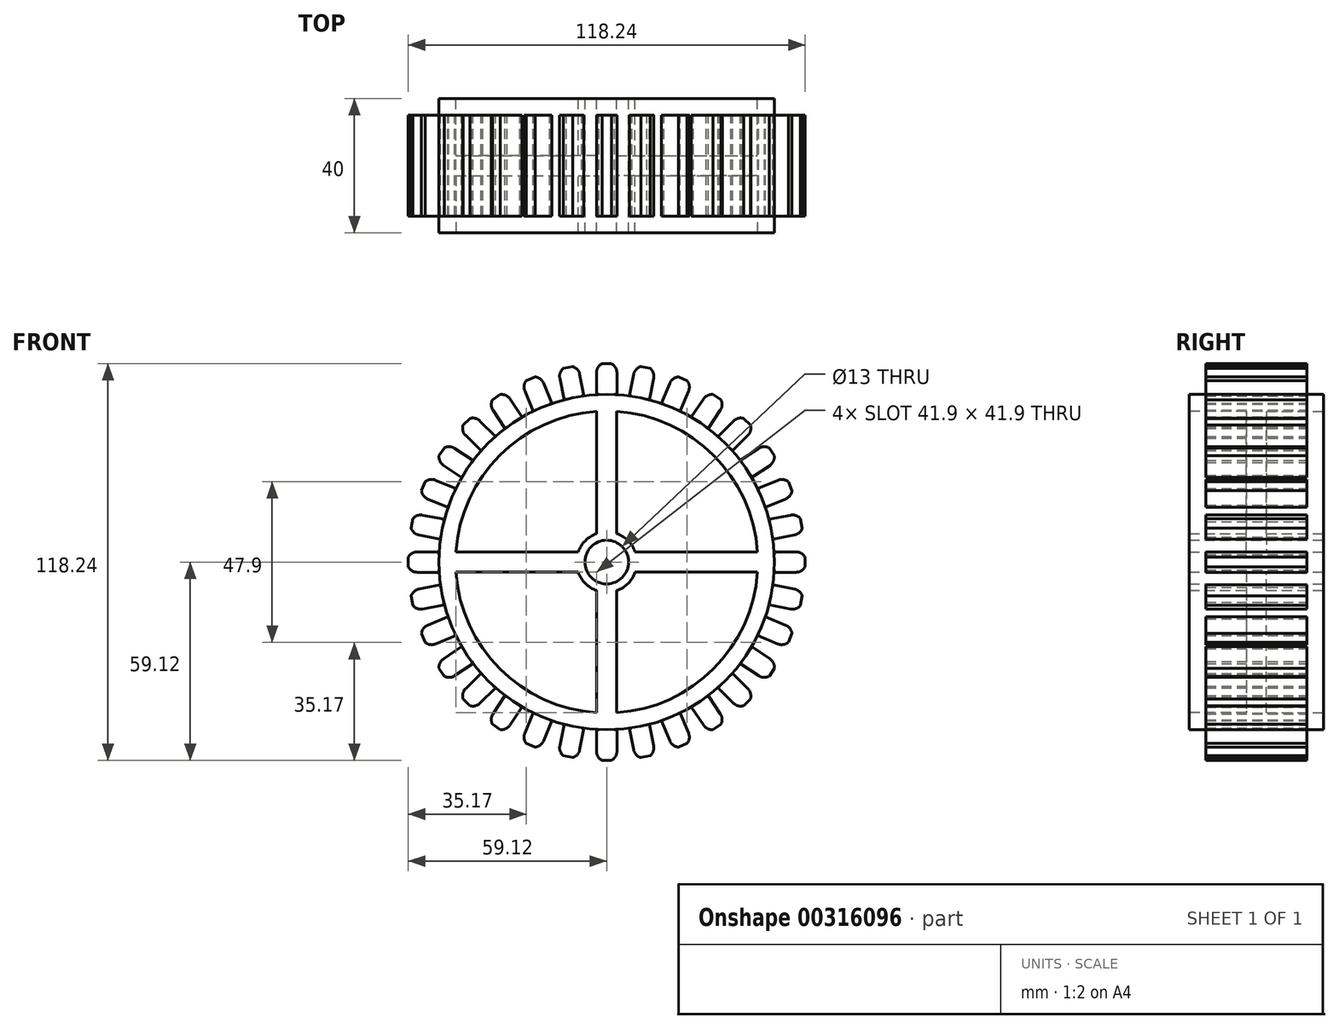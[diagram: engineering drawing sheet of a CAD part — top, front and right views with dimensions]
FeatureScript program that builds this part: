
annotation { "Feature Type Name" : "Feature", "Feature Type Description" : "" }
export const myFeature = defineFeature(function(context is Context, id is Id, definition is map)
    precondition{}
    {
        {
            var Q0;
            Q0=qCreatedBy(makeId("Front.planeOp"),FACE);
            var sketch = newSketch(context, id + "F0", { "sketchPlane" : qUnion([Q0])});
            skCircle(sketch, "E0", {"center": v(0, 0) * mm, "radius": 50 * mm});
            skSolve(sketch);
        }
        {
            var Q0;
            Q0 = qSketchRegion(id + "F0", true);
            extrude(context, id + "F1", {"entities" : qUnion([Q0]), "endBound" : BoundingType.SYMMETRIC, "depth" : 40 * mm});
        }
        {
            var Q0;
            Q0=makeQuery(id+"F1.opExtrude","CAP_FACE",FACE,{"disambiguationData":[OSD([sQuery(id+"F0.wireOp",EDGE,"E0")])],"isStart":false});
            var sketch = newSketch(context, id + "F2", { "sketchPlane" : qUnion([Q0])});
            skArc(sketch, "E1", {"start": v(-44.9, -3) * mm, "mid": v(-31.82, -31.82) * mm, "end": v(-3, -44.9) * mm});
            skLineSegment(sketch, "E2", {"start": v(-44.9, 3) * mm, "end": v(-3, 3) * mm});
            skLineSegment(sketch, "E3", {"start": v(-44.9, -3) * mm, "end": v(-3, -3) * mm});
            skLineSegment(sketch, "E4", {"start": v(-3, 44.9) * mm, "end": v(-3, 3) * mm});
            skLineSegment(sketch, "E5", {"start": v(3, 44.9) * mm, "end": v(3, 3) * mm});
            skArc(sketch, "E6.trimOffspring", {"start": v(-3, 44.9) * mm, "mid": v(-31.82, 31.82) * mm, "end": v(-44.9, 3) * mm});
            skArc(sketch, "E7.trimOffspring", {"start": v(44.9, 3) * mm, "mid": v(31.82, 31.82) * mm, "end": v(3, 44.9) * mm});
            skLineSegment(sketch, "E8.trimOffspring", {"start": v(3, -3) * mm, "end": v(3, -44.9) * mm});
            skLineSegment(sketch, "E9.trimOffspring", {"start": v(3, 3) * mm, "end": v(44.9, 3) * mm});
            skLineSegment(sketch, "E10.trimOffspring", {"start": v(-3, -3) * mm, "end": v(-3, -44.9) * mm});
            skLineSegment(sketch, "E11.trimOffspring", {"start": v(3, -3) * mm, "end": v(44.9, -3) * mm});
            skArc(sketch, "E12.trimOffspring", {"start": v(3, -44.9) * mm, "mid": v(31.82, -31.82) * mm, "end": v(44.9, -3) * mm});
            skLineSegment(sketch, "E13", {"start": v(-3.24, 3) * mm, "end": v(-3, 3.24) * mm});
            skPoint(sketch, "E14.orphan", {"position": v(31.82, 31.82) * mm});
            skPoint(sketch, "E15.orphan", {"position": v(-31.82, -31.82) * mm});
            skSolve(sketch);
        }
        {
            var Q0;
            Q0 = qSketchRegion(id + "F2", true);
            extrude(context, id + "F3", {"entities" : qUnion([Q0]), "operationType" : NewBodyOperationType.REMOVE, "oppositeDirection" : true, "depth" : 17 * mm});
        }
        {
            var Q0;
            Q0=makeQuery(id+"F1.opExtrude","CAP_FACE",FACE,{"disambiguationData":[OSD([sQuery(id+"F0.wireOp",EDGE,"E0")])],"isStart":true});
            var sketch = newSketch(context, id + "F4", { "sketchPlane" : qUnion([Q0])});
            skArc(sketch, "E16", {"start": v(3, -44.9) * mm, "mid": v(31.82, -31.82) * mm, "end": v(44.9, -3) * mm});
            skLineSegment(sketch, "E17", {"start": v(44.9, -3) * mm, "end": v(3, -3) * mm});
            skLineSegment(sketch, "E18", {"start": v(44.9, 3) * mm, "end": v(3, 3) * mm});
            skLineSegment(sketch, "E19", {"start": v(3, -44.9) * mm, "end": v(3, -3) * mm});
            skLineSegment(sketch, "E20", {"start": v(-3, -44.9) * mm, "end": v(-3, -3) * mm});
            skArc(sketch, "E21.trimOffspring", {"start": v(-44.9, -3) * mm, "mid": v(-31.82, -31.82) * mm, "end": v(-3, -44.9) * mm});
            skLineSegment(sketch, "E22.trimOffspring", {"start": v(-3, 3) * mm, "end": v(-3, 44.9) * mm});
            skLineSegment(sketch, "E23.trimOffspring", {"start": v(-3, -3) * mm, "end": v(-44.9, -3) * mm});
            skLineSegment(sketch, "E24.trimOffspring", {"start": v(3, 3) * mm, "end": v(3, 44.9) * mm});
            skLineSegment(sketch, "E25.trimOffspring", {"start": v(-3, 3) * mm, "end": v(-44.9, 3) * mm});
            skArc(sketch, "E26.trimOffspring", {"start": v(44.9, 3) * mm, "mid": v(31.82, 31.82) * mm, "end": v(3, 44.9) * mm});
            skArc(sketch, "E27.trimOffspring", {"start": v(-3, 44.9) * mm, "mid": v(-31.82, 31.82) * mm, "end": v(-44.9, 3) * mm});
            skSolve(sketch);
        }
        {
            var Q0;
            Q0 = qSketchRegion(id + "F4", true);
            var Q1;
            Q1 = qSketchRegion(id + "F6", true);
            extrude(context, id + "F5", {"entities" : qUnion([Q0, Q1]), "operationType" : NewBodyOperationType.REMOVE, "oppositeDirection" : true, "depth" : 17 * mm});
        }
        {
            var Q0;
            Q0=qCreatedBy(makeId("Front.planeOp"),FACE);
            var sketch = newSketch(context, id + "F6", { "sketchPlane" : qUnion([Q0])});
            skLineSegment(sketch, "E28.bottom", {"start": v(-3.03, 49.95) * mm, "end": v(0, 49.95) * mm});
            skLineSegment(sketch, "E28.left", {"start": v(-3.03, 49.95) * mm, "end": v(-3.03, 56.44) * mm});
            skArc(sketch, "E29", {"start": v(-3.03, 56.44) * mm, "mid": v(-2.6, 58) * mm, "end": v(-1.42, 59.12) * mm});
            skLineSegment(sketch, "E30", {"start": v(-1.42, 59.12) * mm, "end": v(0, 59.12) * mm});
            skPoint(sketch, "E31.orphan", {"position": v(0, 59.47) * mm});
            skArc(sketch, "E32.MirrorCS", {"start": v(3.03, 56.44) * mm, "mid": v(2.6, 58) * mm, "end": v(1.42, 59.12) * mm});
            skLineSegment(sketch, "E33.MirrorCS", {"start": v(1.42, 59.12) * mm, "end": v(0, 59.12) * mm});
            skLineSegment(sketch, "E34.MirrorCS", {"start": v(3.03, 49.95) * mm, "end": v(0, 49.95) * mm});
            skLineSegment(sketch, "E35.MirrorCS", {"start": v(3.03, 49.95) * mm, "end": v(3.03, 56.44) * mm});
            skLineSegment(sketch, "E36.1.0", {"start": v(-12.72, 48.4) * mm, "end": v(-13.99, 54.77) * mm});
            skLineSegment(sketch, "E36.1.1", {"start": v(-12.93, 57.7) * mm, "end": v(-11.53, 57.98) * mm});
            skLineSegment(sketch, "E36.1.2", {"start": v(-12.72, 48.4) * mm, "end": v(-9.74, 48.99) * mm});
            skArc(sketch, "E36.1.3", {"start": v(-13.99, 54.77) * mm, "mid": v(-13.87, 56.38) * mm, "end": v(-12.93, 57.7) * mm});
            skArc(sketch, "E36.1.4", {"start": v(-8.04, 55.95) * mm, "mid": v(-8.77, 57.4) * mm, "end": v(-10.14, 58.26) * mm});
            skPoint(sketch, "E36.1.5", {"position": v(-11.6, 58.33) * mm});
            skLineSegment(sketch, "E36.1.6", {"start": v(-6.77, 49.58) * mm, "end": v(-9.74, 48.99) * mm});
            skLineSegment(sketch, "E36.1.7", {"start": v(-6.77, 49.58) * mm, "end": v(-8.04, 55.95) * mm});
            skPoint(sketch, "E36.1.8", {"position": v(-11.6, 58.33) * mm});
            skLineSegment(sketch, "E36.1.9", {"start": v(-10.14, 58.26) * mm, "end": v(-11.53, 57.98) * mm});
            skLineSegment(sketch, "E36.2.0", {"start": v(-21.92, 44.98) * mm, "end": v(-24.4, 50.98) * mm});
            skLineSegment(sketch, "E36.2.1", {"start": v(-23.94, 54.07) * mm, "end": v(-22.62, 54.62) * mm});
            skLineSegment(sketch, "E36.2.2", {"start": v(-21.92, 44.98) * mm, "end": v(-19.11, 46.15) * mm});
            skArc(sketch, "E36.2.3", {"start": v(-24.4, 50.98) * mm, "mid": v(-24.6, 52.6) * mm, "end": v(-23.94, 54.07) * mm});
            skArc(sketch, "E36.2.4", {"start": v(-18.8, 53.3) * mm, "mid": v(-19.8, 54.58) * mm, "end": v(-21.3, 55.16) * mm});
            skPoint(sketch, "E36.2.5", {"position": v(-22.76, 54.95) * mm});
            skLineSegment(sketch, "E36.2.6", {"start": v(-16.31, 47.3) * mm, "end": v(-19.11, 46.15) * mm});
            skLineSegment(sketch, "E36.2.7", {"start": v(-16.31, 47.3) * mm, "end": v(-18.8, 53.3) * mm});
            skPoint(sketch, "E36.2.8", {"position": v(-22.76, 54.95) * mm});
            skLineSegment(sketch, "E36.2.9", {"start": v(-21.3, 55.16) * mm, "end": v(-22.62, 54.62) * mm});
            skLineSegment(sketch, "E36.3.0", {"start": v(-30.27, 39.85) * mm, "end": v(-33.88, 45.24) * mm});
            skLineSegment(sketch, "E36.3.1", {"start": v(-34.03, 48.36) * mm, "end": v(-32.84, 49.16) * mm});
            skLineSegment(sketch, "E36.3.2", {"start": v(-30.27, 39.85) * mm, "end": v(-27.75, 41.53) * mm});
            skArc(sketch, "E36.3.3", {"start": v(-33.88, 45.24) * mm, "mid": v(-34.39, 46.78) * mm, "end": v(-34.03, 48.36) * mm});
            skArc(sketch, "E36.3.4", {"start": v(-28.84, 48.61) * mm, "mid": v(-30.06, 49.67) * mm, "end": v(-31.66, 49.95) * mm});
            skPoint(sketch, "E36.3.5", {"position": v(-33.04, 49.45) * mm});
            skLineSegment(sketch, "E36.3.6", {"start": v(-25.23, 43.21) * mm, "end": v(-27.75, 41.53) * mm});
            skLineSegment(sketch, "E36.3.7", {"start": v(-25.23, 43.21) * mm, "end": v(-28.84, 48.61) * mm});
            skPoint(sketch, "E36.3.8", {"position": v(-33.04, 49.45) * mm});
            skLineSegment(sketch, "E36.3.9", {"start": v(-31.66, 49.95) * mm, "end": v(-32.84, 49.16) * mm});
            skLineSegment(sketch, "E36.4.0", {"start": v(-37.46, 33.17) * mm, "end": v(-42.05, 37.77) * mm});
            skLineSegment(sketch, "E36.4.1", {"start": v(-42.8, 40.8) * mm, "end": v(-41.8, 41.8) * mm});
            skLineSegment(sketch, "E36.4.2", {"start": v(-37.46, 33.17) * mm, "end": v(-35.32, 35.32) * mm});
            skArc(sketch, "E36.4.3", {"start": v(-42.05, 37.77) * mm, "mid": v(-42.85, 39.18) * mm, "end": v(-42.8, 40.8) * mm});
            skArc(sketch, "E36.4.4", {"start": v(-37.77, 42.05) * mm, "mid": v(-39.18, 42.85) * mm, "end": v(-40.8, 42.8) * mm});
            skPoint(sketch, "E36.4.5", {"position": v(-42.05, 42.05) * mm});
            skLineSegment(sketch, "E36.4.6", {"start": v(-33.17, 37.46) * mm, "end": v(-35.32, 35.32) * mm});
            skLineSegment(sketch, "E36.4.7", {"start": v(-33.17, 37.46) * mm, "end": v(-37.77, 42.05) * mm});
            skPoint(sketch, "E36.4.8", {"position": v(-42.05, 42.05) * mm});
            skLineSegment(sketch, "E36.4.9", {"start": v(-40.8, 42.8) * mm, "end": v(-41.8, 41.8) * mm});
            skLineSegment(sketch, "E36.5.0", {"start": v(-43.21, 25.23) * mm, "end": v(-48.61, 28.84) * mm});
            skLineSegment(sketch, "E36.5.1", {"start": v(-49.95, 31.66) * mm, "end": v(-49.16, 32.84) * mm});
            skLineSegment(sketch, "E36.5.2", {"start": v(-43.21, 25.23) * mm, "end": v(-41.53, 27.75) * mm});
            skArc(sketch, "E36.5.3", {"start": v(-48.61, 28.84) * mm, "mid": v(-49.67, 30.06) * mm, "end": v(-49.95, 31.66) * mm});
            skArc(sketch, "E36.5.4", {"start": v(-45.24, 33.88) * mm, "mid": v(-46.78, 34.39) * mm, "end": v(-48.36, 34.03) * mm});
            skPoint(sketch, "E36.5.5", {"position": v(-49.45, 33.04) * mm});
            skLineSegment(sketch, "E36.5.6", {"start": v(-39.85, 30.27) * mm, "end": v(-41.53, 27.75) * mm});
            skLineSegment(sketch, "E36.5.7", {"start": v(-39.85, 30.27) * mm, "end": v(-45.24, 33.88) * mm});
            skPoint(sketch, "E36.5.8", {"position": v(-49.45, 33.04) * mm});
            skLineSegment(sketch, "E36.5.9", {"start": v(-48.36, 34.03) * mm, "end": v(-49.16, 32.84) * mm});
            skLineSegment(sketch, "E36.6.0", {"start": v(-47.3, 16.31) * mm, "end": v(-53.3, 18.8) * mm});
            skLineSegment(sketch, "E36.6.1", {"start": v(-55.16, 21.3) * mm, "end": v(-54.62, 22.62) * mm});
            skLineSegment(sketch, "E36.6.2", {"start": v(-47.3, 16.31) * mm, "end": v(-46.15, 19.11) * mm});
            skArc(sketch, "E36.6.3", {"start": v(-53.3, 18.8) * mm, "mid": v(-54.58, 19.8) * mm, "end": v(-55.16, 21.3) * mm});
            skArc(sketch, "E36.6.4", {"start": v(-50.98, 24.4) * mm, "mid": v(-52.6, 24.6) * mm, "end": v(-54.07, 23.94) * mm});
            skPoint(sketch, "E36.6.5", {"position": v(-54.95, 22.76) * mm});
            skLineSegment(sketch, "E36.6.6", {"start": v(-44.98, 21.92) * mm, "end": v(-46.15, 19.11) * mm});
            skLineSegment(sketch, "E36.6.7", {"start": v(-44.98, 21.92) * mm, "end": v(-50.98, 24.4) * mm});
            skPoint(sketch, "E36.6.8", {"position": v(-54.95, 22.76) * mm});
            skLineSegment(sketch, "E36.6.9", {"start": v(-54.07, 23.94) * mm, "end": v(-54.62, 22.62) * mm});
            skLineSegment(sketch, "E36.7.0", {"start": v(-49.58, 6.77) * mm, "end": v(-55.95, 8.04) * mm});
            skLineSegment(sketch, "E36.7.1", {"start": v(-58.26, 10.14) * mm, "end": v(-57.98, 11.53) * mm});
            skLineSegment(sketch, "E36.7.2", {"start": v(-49.58, 6.77) * mm, "end": v(-48.99, 9.74) * mm});
            skArc(sketch, "E36.7.3", {"start": v(-55.95, 8.04) * mm, "mid": v(-57.4, 8.77) * mm, "end": v(-58.26, 10.14) * mm});
            skArc(sketch, "E36.7.4", {"start": v(-54.77, 13.99) * mm, "mid": v(-56.38, 13.87) * mm, "end": v(-57.7, 12.93) * mm});
            skPoint(sketch, "E36.7.5", {"position": v(-58.33, 11.6) * mm});
            skLineSegment(sketch, "E36.7.6", {"start": v(-48.4, 12.72) * mm, "end": v(-48.99, 9.74) * mm});
            skLineSegment(sketch, "E36.7.7", {"start": v(-48.4, 12.72) * mm, "end": v(-54.77, 13.99) * mm});
            skPoint(sketch, "E36.7.8", {"position": v(-58.33, 11.6) * mm});
            skLineSegment(sketch, "E36.7.9", {"start": v(-57.7, 12.93) * mm, "end": v(-57.98, 11.53) * mm});
            skLineSegment(sketch, "E36.8.0", {"start": v(-49.95, -3.03) * mm, "end": v(-56.44, -3.03) * mm});
            skLineSegment(sketch, "E36.8.1", {"start": v(-59.12, -1.42) * mm, "end": v(-59.12, 0) * mm});
            skLineSegment(sketch, "E36.8.2", {"start": v(-49.95, -3.03) * mm, "end": v(-49.95, 0) * mm});
            skArc(sketch, "E36.8.3", {"start": v(-56.44, -3.03) * mm, "mid": v(-58, -2.6) * mm, "end": v(-59.12, -1.42) * mm});
            skArc(sketch, "E36.8.4", {"start": v(-56.44, 3.03) * mm, "mid": v(-58, 2.6) * mm, "end": v(-59.12, 1.42) * mm});
            skPoint(sketch, "E36.8.5", {"position": v(-59.47, 0) * mm});
            skLineSegment(sketch, "E36.8.6", {"start": v(-49.95, 3.03) * mm, "end": v(-49.95, 0) * mm});
            skLineSegment(sketch, "E36.8.7", {"start": v(-49.95, 3.03) * mm, "end": v(-56.44, 3.03) * mm});
            skPoint(sketch, "E36.8.8", {"position": v(-59.47, 0) * mm});
            skLineSegment(sketch, "E36.8.9", {"start": v(-59.12, 1.42) * mm, "end": v(-59.12, 0) * mm});
            skLineSegment(sketch, "E36.9.0", {"start": v(-48.4, -12.72) * mm, "end": v(-54.77, -13.99) * mm});
            skLineSegment(sketch, "E36.9.1", {"start": v(-57.7, -12.93) * mm, "end": v(-57.98, -11.53) * mm});
            skLineSegment(sketch, "E36.9.2", {"start": v(-48.4, -12.72) * mm, "end": v(-48.99, -9.74) * mm});
            skArc(sketch, "E36.9.3", {"start": v(-54.77, -13.99) * mm, "mid": v(-56.38, -13.87) * mm, "end": v(-57.7, -12.93) * mm});
            skArc(sketch, "E36.9.4", {"start": v(-55.95, -8.04) * mm, "mid": v(-57.4, -8.77) * mm, "end": v(-58.26, -10.14) * mm});
            skPoint(sketch, "E36.9.5", {"position": v(-58.33, -11.6) * mm});
            skLineSegment(sketch, "E36.9.6", {"start": v(-49.58, -6.77) * mm, "end": v(-48.99, -9.74) * mm});
            skLineSegment(sketch, "E36.9.7", {"start": v(-49.58, -6.77) * mm, "end": v(-55.95, -8.04) * mm});
            skPoint(sketch, "E36.9.8", {"position": v(-58.33, -11.6) * mm});
            skLineSegment(sketch, "E36.9.9", {"start": v(-58.26, -10.14) * mm, "end": v(-57.98, -11.53) * mm});
            skLineSegment(sketch, "E36.10.0", {"start": v(-44.98, -21.92) * mm, "end": v(-50.98, -24.4) * mm});
            skLineSegment(sketch, "E36.10.1", {"start": v(-54.07, -23.94) * mm, "end": v(-54.62, -22.62) * mm});
            skLineSegment(sketch, "E36.10.2", {"start": v(-44.98, -21.92) * mm, "end": v(-46.15, -19.11) * mm});
            skArc(sketch, "E36.10.3", {"start": v(-50.98, -24.4) * mm, "mid": v(-52.6, -24.6) * mm, "end": v(-54.07, -23.94) * mm});
            skArc(sketch, "E36.10.4", {"start": v(-53.3, -18.8) * mm, "mid": v(-54.58, -19.8) * mm, "end": v(-55.16, -21.3) * mm});
            skPoint(sketch, "E36.10.5", {"position": v(-54.95, -22.76) * mm});
            skLineSegment(sketch, "E36.10.6", {"start": v(-47.3, -16.31) * mm, "end": v(-46.15, -19.11) * mm});
            skLineSegment(sketch, "E36.10.7", {"start": v(-47.3, -16.31) * mm, "end": v(-53.3, -18.8) * mm});
            skPoint(sketch, "E36.10.8", {"position": v(-54.95, -22.76) * mm});
            skLineSegment(sketch, "E36.10.9", {"start": v(-55.16, -21.3) * mm, "end": v(-54.62, -22.62) * mm});
            skLineSegment(sketch, "E36.11.0", {"start": v(-39.85, -30.27) * mm, "end": v(-45.24, -33.88) * mm});
            skLineSegment(sketch, "E36.11.1", {"start": v(-48.36, -34.03) * mm, "end": v(-49.16, -32.84) * mm});
            skLineSegment(sketch, "E36.11.2", {"start": v(-39.85, -30.27) * mm, "end": v(-41.53, -27.75) * mm});
            skArc(sketch, "E36.11.3", {"start": v(-45.24, -33.88) * mm, "mid": v(-46.78, -34.39) * mm, "end": v(-48.36, -34.03) * mm});
            skArc(sketch, "E36.11.4", {"start": v(-48.61, -28.84) * mm, "mid": v(-49.67, -30.06) * mm, "end": v(-49.95, -31.66) * mm});
            skPoint(sketch, "E36.11.5", {"position": v(-49.45, -33.04) * mm});
            skLineSegment(sketch, "E36.11.6", {"start": v(-43.21, -25.23) * mm, "end": v(-41.53, -27.75) * mm});
            skLineSegment(sketch, "E36.11.7", {"start": v(-43.21, -25.23) * mm, "end": v(-48.61, -28.84) * mm});
            skPoint(sketch, "E36.11.8", {"position": v(-49.45, -33.04) * mm});
            skLineSegment(sketch, "E36.11.9", {"start": v(-49.95, -31.66) * mm, "end": v(-49.16, -32.84) * mm});
            skLineSegment(sketch, "E36.12.0", {"start": v(-33.17, -37.46) * mm, "end": v(-37.77, -42.05) * mm});
            skLineSegment(sketch, "E36.12.1", {"start": v(-40.8, -42.8) * mm, "end": v(-41.8, -41.8) * mm});
            skLineSegment(sketch, "E36.12.2", {"start": v(-33.17, -37.46) * mm, "end": v(-35.32, -35.32) * mm});
            skArc(sketch, "E36.12.3", {"start": v(-37.77, -42.05) * mm, "mid": v(-39.18, -42.85) * mm, "end": v(-40.8, -42.8) * mm});
            skArc(sketch, "E36.12.4", {"start": v(-42.05, -37.77) * mm, "mid": v(-42.85, -39.18) * mm, "end": v(-42.8, -40.8) * mm});
            skPoint(sketch, "E36.12.5", {"position": v(-42.05, -42.05) * mm});
            skLineSegment(sketch, "E36.12.6", {"start": v(-37.46, -33.17) * mm, "end": v(-35.32, -35.32) * mm});
            skLineSegment(sketch, "E36.12.7", {"start": v(-37.46, -33.17) * mm, "end": v(-42.05, -37.77) * mm});
            skPoint(sketch, "E36.12.8", {"position": v(-42.05, -42.05) * mm});
            skLineSegment(sketch, "E36.12.9", {"start": v(-42.8, -40.8) * mm, "end": v(-41.8, -41.8) * mm});
            skLineSegment(sketch, "E36.13.0", {"start": v(-25.23, -43.21) * mm, "end": v(-28.84, -48.61) * mm});
            skLineSegment(sketch, "E36.13.1", {"start": v(-31.66, -49.95) * mm, "end": v(-32.84, -49.16) * mm});
            skLineSegment(sketch, "E36.13.2", {"start": v(-25.23, -43.21) * mm, "end": v(-27.75, -41.53) * mm});
            skArc(sketch, "E36.13.3", {"start": v(-28.84, -48.61) * mm, "mid": v(-30.06, -49.67) * mm, "end": v(-31.66, -49.95) * mm});
            skArc(sketch, "E36.13.4", {"start": v(-33.88, -45.24) * mm, "mid": v(-34.39, -46.78) * mm, "end": v(-34.03, -48.36) * mm});
            skPoint(sketch, "E36.13.5", {"position": v(-33.04, -49.45) * mm});
            skLineSegment(sketch, "E36.13.6", {"start": v(-30.27, -39.85) * mm, "end": v(-27.75, -41.53) * mm});
            skLineSegment(sketch, "E36.13.7", {"start": v(-30.27, -39.85) * mm, "end": v(-33.88, -45.24) * mm});
            skPoint(sketch, "E36.13.8", {"position": v(-33.04, -49.45) * mm});
            skLineSegment(sketch, "E36.13.9", {"start": v(-34.03, -48.36) * mm, "end": v(-32.84, -49.16) * mm});
            skLineSegment(sketch, "E36.14.0", {"start": v(-16.31, -47.3) * mm, "end": v(-18.8, -53.3) * mm});
            skLineSegment(sketch, "E36.14.1", {"start": v(-21.3, -55.16) * mm, "end": v(-22.62, -54.62) * mm});
            skLineSegment(sketch, "E36.14.2", {"start": v(-16.31, -47.3) * mm, "end": v(-19.11, -46.15) * mm});
            skArc(sketch, "E36.14.3", {"start": v(-18.8, -53.3) * mm, "mid": v(-19.8, -54.58) * mm, "end": v(-21.3, -55.16) * mm});
            skArc(sketch, "E36.14.4", {"start": v(-24.4, -50.98) * mm, "mid": v(-24.6, -52.6) * mm, "end": v(-23.94, -54.07) * mm});
            skPoint(sketch, "E36.14.5", {"position": v(-22.76, -54.95) * mm});
            skLineSegment(sketch, "E36.14.6", {"start": v(-21.92, -44.98) * mm, "end": v(-19.11, -46.15) * mm});
            skLineSegment(sketch, "E36.14.7", {"start": v(-21.92, -44.98) * mm, "end": v(-24.4, -50.98) * mm});
            skPoint(sketch, "E36.14.8", {"position": v(-22.76, -54.95) * mm});
            skLineSegment(sketch, "E36.14.9", {"start": v(-23.94, -54.07) * mm, "end": v(-22.62, -54.62) * mm});
            skLineSegment(sketch, "E36.15.0", {"start": v(-6.77, -49.58) * mm, "end": v(-8.04, -55.95) * mm});
            skLineSegment(sketch, "E36.15.1", {"start": v(-10.14, -58.26) * mm, "end": v(-11.53, -57.98) * mm});
            skLineSegment(sketch, "E36.15.2", {"start": v(-6.77, -49.58) * mm, "end": v(-9.74, -48.99) * mm});
            skArc(sketch, "E36.15.3", {"start": v(-8.04, -55.95) * mm, "mid": v(-8.77, -57.4) * mm, "end": v(-10.14, -58.26) * mm});
            skArc(sketch, "E36.15.4", {"start": v(-13.99, -54.77) * mm, "mid": v(-13.87, -56.38) * mm, "end": v(-12.93, -57.7) * mm});
            skPoint(sketch, "E36.15.5", {"position": v(-11.6, -58.33) * mm});
            skLineSegment(sketch, "E36.15.6", {"start": v(-12.72, -48.4) * mm, "end": v(-9.74, -48.99) * mm});
            skLineSegment(sketch, "E36.15.7", {"start": v(-12.72, -48.4) * mm, "end": v(-13.99, -54.77) * mm});
            skPoint(sketch, "E36.15.8", {"position": v(-11.6, -58.33) * mm});
            skLineSegment(sketch, "E36.15.9", {"start": v(-12.93, -57.7) * mm, "end": v(-11.53, -57.98) * mm});
            skLineSegment(sketch, "E36.16.0", {"start": v(3.03, -49.95) * mm, "end": v(3.03, -56.44) * mm});
            skLineSegment(sketch, "E36.16.1", {"start": v(1.42, -59.12) * mm, "end": v(0, -59.12) * mm});
            skLineSegment(sketch, "E36.16.2", {"start": v(3.03, -49.95) * mm, "end": v(0, -49.95) * mm});
            skArc(sketch, "E36.16.3", {"start": v(3.03, -56.44) * mm, "mid": v(2.6, -58) * mm, "end": v(1.42, -59.12) * mm});
            skArc(sketch, "E36.16.4", {"start": v(-3.03, -56.44) * mm, "mid": v(-2.6, -58) * mm, "end": v(-1.42, -59.12) * mm});
            skPoint(sketch, "E36.16.5", {"position": v(0, -59.47) * mm});
            skLineSegment(sketch, "E36.16.6", {"start": v(-3.03, -49.95) * mm, "end": v(0, -49.95) * mm});
            skLineSegment(sketch, "E36.16.7", {"start": v(-3.03, -49.95) * mm, "end": v(-3.03, -56.44) * mm});
            skPoint(sketch, "E36.16.8", {"position": v(0, -59.47) * mm});
            skLineSegment(sketch, "E36.16.9", {"start": v(-1.42, -59.12) * mm, "end": v(0, -59.12) * mm});
            skLineSegment(sketch, "E36.17.0", {"start": v(12.72, -48.4) * mm, "end": v(13.99, -54.77) * mm});
            skLineSegment(sketch, "E36.17.1", {"start": v(12.93, -57.7) * mm, "end": v(11.53, -57.98) * mm});
            skLineSegment(sketch, "E36.17.2", {"start": v(12.72, -48.4) * mm, "end": v(9.74, -48.99) * mm});
            skArc(sketch, "E36.17.3", {"start": v(13.99, -54.77) * mm, "mid": v(13.87, -56.38) * mm, "end": v(12.93, -57.7) * mm});
            skArc(sketch, "E36.17.4", {"start": v(8.04, -55.95) * mm, "mid": v(8.77, -57.4) * mm, "end": v(10.14, -58.26) * mm});
            skPoint(sketch, "E36.17.5", {"position": v(11.6, -58.33) * mm});
            skLineSegment(sketch, "E36.17.6", {"start": v(6.77, -49.58) * mm, "end": v(9.74, -48.99) * mm});
            skLineSegment(sketch, "E36.17.7", {"start": v(6.77, -49.58) * mm, "end": v(8.04, -55.95) * mm});
            skPoint(sketch, "E36.17.8", {"position": v(11.6, -58.33) * mm});
            skLineSegment(sketch, "E36.17.9", {"start": v(10.14, -58.26) * mm, "end": v(11.53, -57.98) * mm});
            skLineSegment(sketch, "E36.18.0", {"start": v(21.92, -44.98) * mm, "end": v(24.4, -50.98) * mm});
            skLineSegment(sketch, "E36.18.1", {"start": v(23.94, -54.07) * mm, "end": v(22.62, -54.62) * mm});
            skLineSegment(sketch, "E36.18.2", {"start": v(21.92, -44.98) * mm, "end": v(19.11, -46.15) * mm});
            skArc(sketch, "E36.18.3", {"start": v(24.4, -50.98) * mm, "mid": v(24.6, -52.6) * mm, "end": v(23.94, -54.07) * mm});
            skArc(sketch, "E36.18.4", {"start": v(18.8, -53.3) * mm, "mid": v(19.8, -54.58) * mm, "end": v(21.3, -55.16) * mm});
            skPoint(sketch, "E36.18.5", {"position": v(22.76, -54.95) * mm});
            skLineSegment(sketch, "E36.18.6", {"start": v(16.31, -47.3) * mm, "end": v(19.11, -46.15) * mm});
            skLineSegment(sketch, "E36.18.7", {"start": v(16.31, -47.3) * mm, "end": v(18.8, -53.3) * mm});
            skPoint(sketch, "E36.18.8", {"position": v(22.76, -54.95) * mm});
            skLineSegment(sketch, "E36.18.9", {"start": v(21.3, -55.16) * mm, "end": v(22.62, -54.62) * mm});
            skLineSegment(sketch, "E36.19.0", {"start": v(30.27, -39.85) * mm, "end": v(33.88, -45.24) * mm});
            skLineSegment(sketch, "E36.19.1", {"start": v(34.03, -48.36) * mm, "end": v(32.84, -49.16) * mm});
            skLineSegment(sketch, "E36.19.2", {"start": v(30.27, -39.85) * mm, "end": v(27.75, -41.53) * mm});
            skArc(sketch, "E36.19.3", {"start": v(33.88, -45.24) * mm, "mid": v(34.39, -46.78) * mm, "end": v(34.03, -48.36) * mm});
            skArc(sketch, "E36.19.4", {"start": v(28.84, -48.61) * mm, "mid": v(30.06, -49.67) * mm, "end": v(31.66, -49.95) * mm});
            skPoint(sketch, "E36.19.5", {"position": v(33.04, -49.45) * mm});
            skLineSegment(sketch, "E36.19.6", {"start": v(25.23, -43.21) * mm, "end": v(27.75, -41.53) * mm});
            skLineSegment(sketch, "E36.19.7", {"start": v(25.23, -43.21) * mm, "end": v(28.84, -48.61) * mm});
            skPoint(sketch, "E36.19.8", {"position": v(33.04, -49.45) * mm});
            skLineSegment(sketch, "E36.19.9", {"start": v(31.66, -49.95) * mm, "end": v(32.84, -49.16) * mm});
            skLineSegment(sketch, "E36.20.0", {"start": v(37.46, -33.17) * mm, "end": v(42.05, -37.77) * mm});
            skLineSegment(sketch, "E36.20.1", {"start": v(42.8, -40.8) * mm, "end": v(41.8, -41.8) * mm});
            skLineSegment(sketch, "E36.20.2", {"start": v(37.46, -33.17) * mm, "end": v(35.32, -35.32) * mm});
            skArc(sketch, "E36.20.3", {"start": v(42.05, -37.77) * mm, "mid": v(42.85, -39.18) * mm, "end": v(42.8, -40.8) * mm});
            skArc(sketch, "E36.20.4", {"start": v(37.77, -42.05) * mm, "mid": v(39.18, -42.85) * mm, "end": v(40.8, -42.8) * mm});
            skPoint(sketch, "E36.20.5", {"position": v(42.05, -42.05) * mm});
            skLineSegment(sketch, "E36.20.6", {"start": v(33.17, -37.46) * mm, "end": v(35.32, -35.32) * mm});
            skLineSegment(sketch, "E36.20.7", {"start": v(33.17, -37.46) * mm, "end": v(37.77, -42.05) * mm});
            skPoint(sketch, "E36.20.8", {"position": v(42.05, -42.05) * mm});
            skLineSegment(sketch, "E36.20.9", {"start": v(40.8, -42.8) * mm, "end": v(41.8, -41.8) * mm});
            skLineSegment(sketch, "E36.21.0", {"start": v(43.21, -25.23) * mm, "end": v(48.61, -28.84) * mm});
            skLineSegment(sketch, "E36.21.1", {"start": v(49.95, -31.66) * mm, "end": v(49.16, -32.84) * mm});
            skLineSegment(sketch, "E36.21.2", {"start": v(43.21, -25.23) * mm, "end": v(41.53, -27.75) * mm});
            skArc(sketch, "E36.21.3", {"start": v(48.61, -28.84) * mm, "mid": v(49.67, -30.06) * mm, "end": v(49.95, -31.66) * mm});
            skArc(sketch, "E36.21.4", {"start": v(45.24, -33.88) * mm, "mid": v(46.78, -34.39) * mm, "end": v(48.36, -34.03) * mm});
            skPoint(sketch, "E36.21.5", {"position": v(49.45, -33.04) * mm});
            skLineSegment(sketch, "E36.21.6", {"start": v(39.85, -30.27) * mm, "end": v(41.53, -27.75) * mm});
            skLineSegment(sketch, "E36.21.7", {"start": v(39.85, -30.27) * mm, "end": v(45.24, -33.88) * mm});
            skPoint(sketch, "E36.21.8", {"position": v(49.45, -33.04) * mm});
            skLineSegment(sketch, "E36.21.9", {"start": v(48.36, -34.03) * mm, "end": v(49.16, -32.84) * mm});
            skLineSegment(sketch, "E36.22.0", {"start": v(47.3, -16.31) * mm, "end": v(53.3, -18.8) * mm});
            skLineSegment(sketch, "E36.22.1", {"start": v(55.16, -21.3) * mm, "end": v(54.62, -22.62) * mm});
            skLineSegment(sketch, "E36.22.2", {"start": v(47.3, -16.31) * mm, "end": v(46.15, -19.11) * mm});
            skArc(sketch, "E36.22.3", {"start": v(53.3, -18.8) * mm, "mid": v(54.58, -19.8) * mm, "end": v(55.16, -21.3) * mm});
            skArc(sketch, "E36.22.4", {"start": v(50.98, -24.4) * mm, "mid": v(52.6, -24.6) * mm, "end": v(54.07, -23.94) * mm});
            skPoint(sketch, "E36.22.5", {"position": v(54.95, -22.76) * mm});
            skLineSegment(sketch, "E36.22.6", {"start": v(44.98, -21.92) * mm, "end": v(46.15, -19.11) * mm});
            skLineSegment(sketch, "E36.22.7", {"start": v(44.98, -21.92) * mm, "end": v(50.98, -24.4) * mm});
            skPoint(sketch, "E36.22.8", {"position": v(54.95, -22.76) * mm});
            skLineSegment(sketch, "E36.22.9", {"start": v(54.07, -23.94) * mm, "end": v(54.62, -22.62) * mm});
            skLineSegment(sketch, "E36.23.0", {"start": v(49.58, -6.77) * mm, "end": v(55.95, -8.04) * mm});
            skLineSegment(sketch, "E36.23.1", {"start": v(58.26, -10.14) * mm, "end": v(57.98, -11.53) * mm});
            skLineSegment(sketch, "E36.23.2", {"start": v(49.58, -6.77) * mm, "end": v(48.99, -9.74) * mm});
            skArc(sketch, "E36.23.3", {"start": v(55.95, -8.04) * mm, "mid": v(57.4, -8.77) * mm, "end": v(58.26, -10.14) * mm});
            skArc(sketch, "E36.23.4", {"start": v(54.77, -13.99) * mm, "mid": v(56.38, -13.87) * mm, "end": v(57.7, -12.93) * mm});
            skPoint(sketch, "E36.23.5", {"position": v(58.33, -11.6) * mm});
            skLineSegment(sketch, "E36.23.6", {"start": v(48.4, -12.72) * mm, "end": v(48.99, -9.74) * mm});
            skLineSegment(sketch, "E36.23.7", {"start": v(48.4, -12.72) * mm, "end": v(54.77, -13.99) * mm});
            skPoint(sketch, "E36.23.8", {"position": v(58.33, -11.6) * mm});
            skLineSegment(sketch, "E36.23.9", {"start": v(57.7, -12.93) * mm, "end": v(57.98, -11.53) * mm});
            skLineSegment(sketch, "E36.24.0", {"start": v(49.95, 3.03) * mm, "end": v(56.44, 3.03) * mm});
            skLineSegment(sketch, "E36.24.1", {"start": v(59.12, 1.42) * mm, "end": v(59.12, 0) * mm});
            skLineSegment(sketch, "E36.24.2", {"start": v(49.95, 3.03) * mm, "end": v(49.95, 0) * mm});
            skArc(sketch, "E36.24.3", {"start": v(56.44, 3.03) * mm, "mid": v(58, 2.6) * mm, "end": v(59.12, 1.42) * mm});
            skArc(sketch, "E36.24.4", {"start": v(56.44, -3.03) * mm, "mid": v(58, -2.6) * mm, "end": v(59.12, -1.42) * mm});
            skPoint(sketch, "E36.24.5", {"position": v(59.47, 0) * mm});
            skLineSegment(sketch, "E36.24.6", {"start": v(49.95, -3.03) * mm, "end": v(49.95, 0) * mm});
            skLineSegment(sketch, "E36.24.7", {"start": v(49.95, -3.03) * mm, "end": v(56.44, -3.03) * mm});
            skPoint(sketch, "E36.24.8", {"position": v(59.47, 0) * mm});
            skLineSegment(sketch, "E36.24.9", {"start": v(59.12, -1.42) * mm, "end": v(59.12, 0) * mm});
            skLineSegment(sketch, "E36.25.0", {"start": v(48.4, 12.72) * mm, "end": v(54.77, 13.99) * mm});
            skLineSegment(sketch, "E36.25.1", {"start": v(57.7, 12.93) * mm, "end": v(57.98, 11.53) * mm});
            skLineSegment(sketch, "E36.25.2", {"start": v(48.4, 12.72) * mm, "end": v(48.99, 9.74) * mm});
            skArc(sketch, "E36.25.3", {"start": v(54.77, 13.99) * mm, "mid": v(56.38, 13.87) * mm, "end": v(57.7, 12.93) * mm});
            skArc(sketch, "E36.25.4", {"start": v(55.95, 8.04) * mm, "mid": v(57.4, 8.77) * mm, "end": v(58.26, 10.14) * mm});
            skPoint(sketch, "E36.25.5", {"position": v(58.33, 11.6) * mm});
            skLineSegment(sketch, "E36.25.6", {"start": v(49.58, 6.77) * mm, "end": v(48.99, 9.74) * mm});
            skLineSegment(sketch, "E36.25.7", {"start": v(49.58, 6.77) * mm, "end": v(55.95, 8.04) * mm});
            skPoint(sketch, "E36.25.8", {"position": v(58.33, 11.6) * mm});
            skLineSegment(sketch, "E36.25.9", {"start": v(58.26, 10.14) * mm, "end": v(57.98, 11.53) * mm});
            skLineSegment(sketch, "E36.26.0", {"start": v(44.98, 21.92) * mm, "end": v(50.98, 24.4) * mm});
            skLineSegment(sketch, "E36.26.1", {"start": v(54.07, 23.94) * mm, "end": v(54.62, 22.62) * mm});
            skLineSegment(sketch, "E36.26.2", {"start": v(44.98, 21.92) * mm, "end": v(46.15, 19.11) * mm});
            skArc(sketch, "E36.26.3", {"start": v(50.98, 24.4) * mm, "mid": v(52.6, 24.6) * mm, "end": v(54.07, 23.94) * mm});
            skArc(sketch, "E36.26.4", {"start": v(53.3, 18.8) * mm, "mid": v(54.58, 19.8) * mm, "end": v(55.16, 21.3) * mm});
            skPoint(sketch, "E36.26.5", {"position": v(54.95, 22.76) * mm});
            skLineSegment(sketch, "E36.26.6", {"start": v(47.3, 16.31) * mm, "end": v(46.15, 19.11) * mm});
            skLineSegment(sketch, "E36.26.7", {"start": v(47.3, 16.31) * mm, "end": v(53.3, 18.8) * mm});
            skPoint(sketch, "E36.26.8", {"position": v(54.95, 22.76) * mm});
            skLineSegment(sketch, "E36.26.9", {"start": v(55.16, 21.3) * mm, "end": v(54.62, 22.62) * mm});
            skLineSegment(sketch, "E36.27.0", {"start": v(39.85, 30.27) * mm, "end": v(45.24, 33.88) * mm});
            skLineSegment(sketch, "E36.27.1", {"start": v(48.36, 34.03) * mm, "end": v(49.16, 32.84) * mm});
            skLineSegment(sketch, "E36.27.2", {"start": v(39.85, 30.27) * mm, "end": v(41.53, 27.75) * mm});
            skArc(sketch, "E36.27.3", {"start": v(45.24, 33.88) * mm, "mid": v(46.78, 34.39) * mm, "end": v(48.36, 34.03) * mm});
            skArc(sketch, "E36.27.4", {"start": v(48.61, 28.84) * mm, "mid": v(49.67, 30.06) * mm, "end": v(49.95, 31.66) * mm});
            skPoint(sketch, "E36.27.5", {"position": v(49.45, 33.04) * mm});
            skLineSegment(sketch, "E36.27.6", {"start": v(43.21, 25.23) * mm, "end": v(41.53, 27.75) * mm});
            skLineSegment(sketch, "E36.27.7", {"start": v(43.21, 25.23) * mm, "end": v(48.61, 28.84) * mm});
            skPoint(sketch, "E36.27.8", {"position": v(49.45, 33.04) * mm});
            skLineSegment(sketch, "E36.27.9", {"start": v(49.95, 31.66) * mm, "end": v(49.16, 32.84) * mm});
            skLineSegment(sketch, "E36.28.0", {"start": v(33.17, 37.46) * mm, "end": v(37.77, 42.05) * mm});
            skLineSegment(sketch, "E36.28.1", {"start": v(40.8, 42.8) * mm, "end": v(41.8, 41.8) * mm});
            skLineSegment(sketch, "E36.28.2", {"start": v(33.17, 37.46) * mm, "end": v(35.32, 35.32) * mm});
            skArc(sketch, "E36.28.3", {"start": v(37.77, 42.05) * mm, "mid": v(39.18, 42.85) * mm, "end": v(40.8, 42.8) * mm});
            skArc(sketch, "E36.28.4", {"start": v(42.05, 37.77) * mm, "mid": v(42.85, 39.18) * mm, "end": v(42.8, 40.8) * mm});
            skPoint(sketch, "E36.28.5", {"position": v(42.05, 42.05) * mm});
            skLineSegment(sketch, "E36.28.6", {"start": v(37.46, 33.17) * mm, "end": v(35.32, 35.32) * mm});
            skLineSegment(sketch, "E36.28.7", {"start": v(37.46, 33.17) * mm, "end": v(42.05, 37.77) * mm});
            skPoint(sketch, "E36.28.8", {"position": v(42.05, 42.05) * mm});
            skLineSegment(sketch, "E36.28.9", {"start": v(42.8, 40.8) * mm, "end": v(41.8, 41.8) * mm});
            skLineSegment(sketch, "E36.29.0", {"start": v(25.23, 43.21) * mm, "end": v(28.84, 48.61) * mm});
            skLineSegment(sketch, "E36.29.1", {"start": v(31.66, 49.95) * mm, "end": v(32.84, 49.16) * mm});
            skLineSegment(sketch, "E36.29.2", {"start": v(25.23, 43.21) * mm, "end": v(27.75, 41.53) * mm});
            skArc(sketch, "E36.29.3", {"start": v(28.84, 48.61) * mm, "mid": v(30.06, 49.67) * mm, "end": v(31.66, 49.95) * mm});
            skArc(sketch, "E36.29.4", {"start": v(33.88, 45.24) * mm, "mid": v(34.39, 46.78) * mm, "end": v(34.03, 48.36) * mm});
            skPoint(sketch, "E36.29.5", {"position": v(33.04, 49.45) * mm});
            skLineSegment(sketch, "E36.29.6", {"start": v(30.27, 39.85) * mm, "end": v(27.75, 41.53) * mm});
            skLineSegment(sketch, "E36.29.7", {"start": v(30.27, 39.85) * mm, "end": v(33.88, 45.24) * mm});
            skPoint(sketch, "E36.29.8", {"position": v(33.04, 49.45) * mm});
            skLineSegment(sketch, "E36.29.9", {"start": v(34.03, 48.36) * mm, "end": v(32.84, 49.16) * mm});
            skLineSegment(sketch, "E36.30.0", {"start": v(16.31, 47.3) * mm, "end": v(18.8, 53.3) * mm});
            skLineSegment(sketch, "E36.30.1", {"start": v(21.3, 55.16) * mm, "end": v(22.62, 54.62) * mm});
            skLineSegment(sketch, "E36.30.2", {"start": v(16.31, 47.3) * mm, "end": v(19.11, 46.15) * mm});
            skArc(sketch, "E36.30.3", {"start": v(18.8, 53.3) * mm, "mid": v(19.8, 54.58) * mm, "end": v(21.3, 55.16) * mm});
            skArc(sketch, "E36.30.4", {"start": v(24.4, 50.98) * mm, "mid": v(24.6, 52.6) * mm, "end": v(23.94, 54.07) * mm});
            skPoint(sketch, "E36.30.5", {"position": v(22.76, 54.95) * mm});
            skLineSegment(sketch, "E36.30.6", {"start": v(21.92, 44.98) * mm, "end": v(19.11, 46.15) * mm});
            skLineSegment(sketch, "E36.30.7", {"start": v(21.92, 44.98) * mm, "end": v(24.4, 50.98) * mm});
            skPoint(sketch, "E36.30.8", {"position": v(22.76, 54.95) * mm});
            skLineSegment(sketch, "E36.30.9", {"start": v(23.94, 54.07) * mm, "end": v(22.62, 54.62) * mm});
            skLineSegment(sketch, "E36.31.0", {"start": v(6.77, 49.58) * mm, "end": v(8.04, 55.95) * mm});
            skLineSegment(sketch, "E36.31.1", {"start": v(10.14, 58.26) * mm, "end": v(11.53, 57.98) * mm});
            skLineSegment(sketch, "E36.31.2", {"start": v(6.77, 49.58) * mm, "end": v(9.74, 48.99) * mm});
            skArc(sketch, "E36.31.3", {"start": v(8.04, 55.95) * mm, "mid": v(8.77, 57.4) * mm, "end": v(10.14, 58.26) * mm});
            skArc(sketch, "E36.31.4", {"start": v(13.99, 54.77) * mm, "mid": v(13.87, 56.38) * mm, "end": v(12.93, 57.7) * mm});
            skPoint(sketch, "E36.31.5", {"position": v(11.6, 58.33) * mm});
            skLineSegment(sketch, "E36.31.6", {"start": v(12.72, 48.4) * mm, "end": v(9.74, 48.99) * mm});
            skLineSegment(sketch, "E36.31.7", {"start": v(12.72, 48.4) * mm, "end": v(13.99, 54.77) * mm});
            skPoint(sketch, "E36.31.8", {"position": v(11.6, 58.33) * mm});
            skLineSegment(sketch, "E36.31.9", {"start": v(12.93, 57.7) * mm, "end": v(11.53, 57.98) * mm});
            skPoint(sketch, "E36.center", {"position": v(0, 0) * mm});
            skSolve(sketch);
        }
        {
            var Q0;
            Q0 = qSketchRegion(id + "F6", true);
            extrude(context, id + "F7", {"entities" : qUnion([Q0]), "operationType" : NewBodyOperationType.ADD, "endBound" : BoundingType.SYMMETRIC, "depth" : 30 * mm});
        }
        {
            var Q0;
            Q0=qCreatedBy(makeId("Front.planeOp"),FACE);
            var sketch = newSketch(context, id + "F8", { "sketchPlane" : qUnion([Q0])});
            skCircle(sketch, "E37", {"center": v(0, 0) * mm, "radius": 6.5 * mm});
            skCircle(sketch, "E38", {"center": v(0, 0) * mm, "radius": 9 * mm});
            skSolve(sketch);
        }
        {
            var Q0;
            Q0 = qSketchRegion(id + "F8", true);
            extrude(context, id + "F9", {"entities" : qUnion([Q0]), "operationType" : NewBodyOperationType.ADD, "endBound" : BoundingType.SYMMETRIC, "depth" : 40 * mm});
        }
        {
            var Q0;
            Q0=qCreatedBy(makeId("Front.planeOp"),FACE);
            var sketch = newSketch(context, id + "F10", { "sketchPlane" : qUnion([Q0])});
            skCircle(sketch, "E39", {"center": v(0, 0) * mm, "radius": 6.5 * mm});
            skSolve(sketch);
        }
        {
            var Q0;
            Q0 = qSketchRegion(id + "F10", true);
            extrude(context, id + "F11", {"entities" : qUnion([Q0]), "operationType" : NewBodyOperationType.REMOVE, "endBound" : BoundingType.SYMMETRIC, "oppositeDirection" : true, "depth" : 42 * mm});
        }
    });
